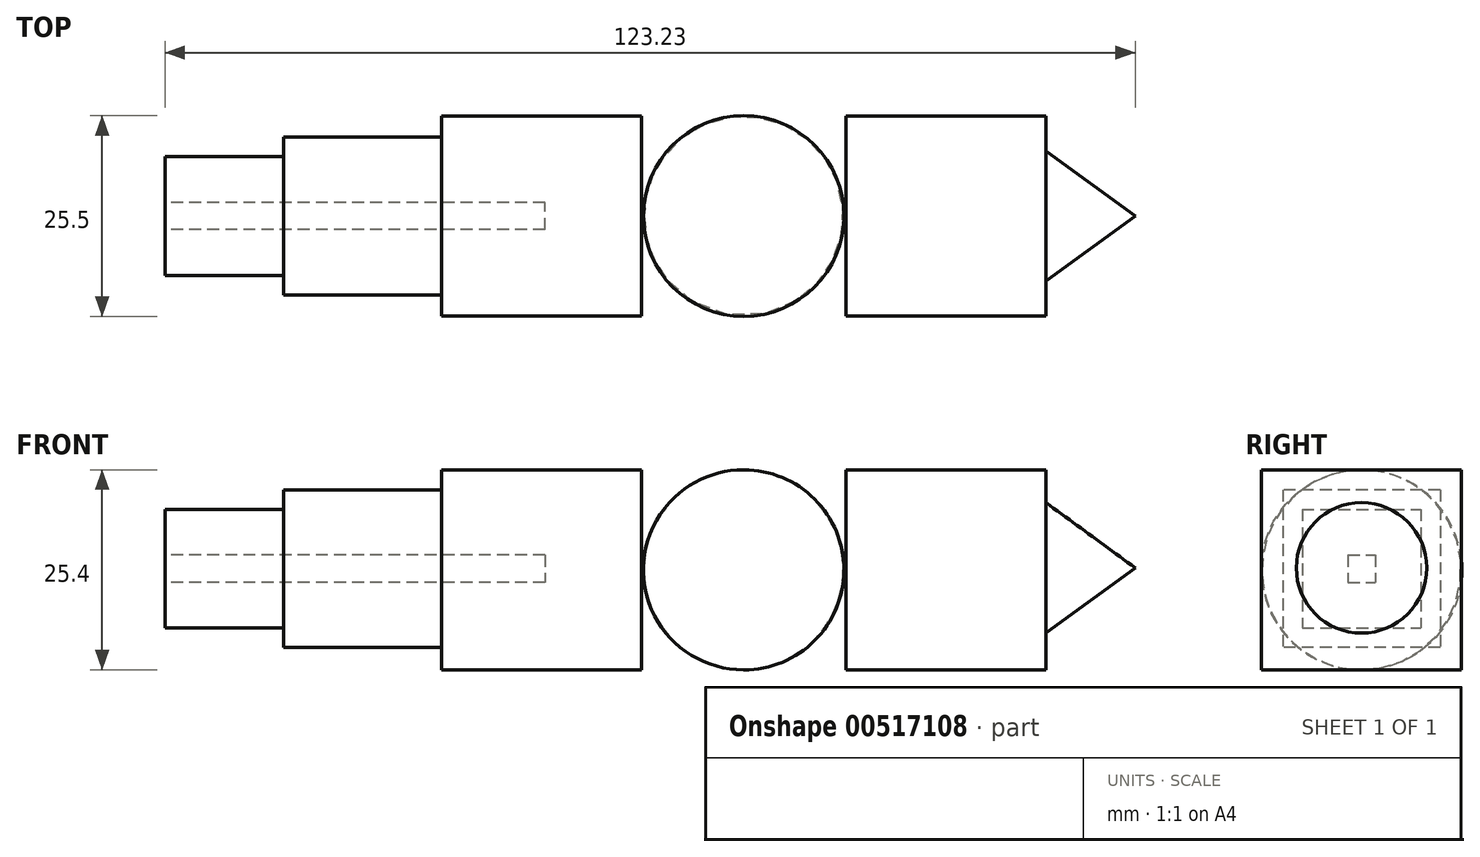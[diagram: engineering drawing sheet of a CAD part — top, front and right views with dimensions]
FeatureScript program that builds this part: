
annotation { "Feature Type Name" : "Feature", "Feature Type Description" : "" }
export const myFeature = defineFeature(function(context is Context, id is Id, definition is map)
    precondition{}
    {
        {
            var Q0;
            Q0=qCreatedBy(makeId("Front.planeOp"),FACE);
            var sketch = newSketch(context, id + "F0", { "sketchPlane" : qUnion([Q0])});
            skLineSegment(sketch, "E0.bottom", {"start": v(-38.4, 25.4) * mm, "end": v(-13, 25.4) * mm});
            skLineSegment(sketch, "E0.top", {"start": v(-38.4, 0) * mm, "end": v(-13, 0) * mm});
            skLineSegment(sketch, "E0.left", {"start": v(-38.4, 25.4) * mm, "end": v(-38.4, 0) * mm});
            skLineSegment(sketch, "E0.right", {"start": v(-13, 25.4) * mm, "end": v(-13, 0) * mm});
            skLineSegment(sketch, "E1", {"start": v(0, 25.4) * mm, "end": v(0, 0) * mm});
            skArc(sketch, "E2", {"start": v(0, 0) * mm, "mid": v(12.65, 12.7) * mm, "end": v(0, 25.4) * mm});
            skLineSegment(sketch, "E3.bottom", {"start": v(13, 25.4) * mm, "end": v(38.4, 25.4) * mm});
            skLineSegment(sketch, "E3.top", {"start": v(13, 0) * mm, "end": v(38.4, 0) * mm});
            skLineSegment(sketch, "E3.left", {"start": v(13, 25.4) * mm, "end": v(13, 0) * mm});
            skLineSegment(sketch, "E3.right", {"start": v(38.4, 25.4) * mm, "end": v(38.4, 0) * mm});
            skSolve(sketch);
        }
        {
            var Q0;
            Q0=makeQuery(id+"F0.imprint","IMPRINT",FACE,{"disambiguationData":[TD([[makeQuery(id+"F0.imprint","IMPRINT",EDGE,{"derivedFrom":sQuery(id+"F0.wireOp",EDGE,"E1")}),1.0]])]});
            var Q1;
            Q1=sQuery(id+"F0.wireOp",EDGE,"E1");
            revolve(context, id + "F1", {"entities" : qUnion([Q0]), "axis" : qUnion([Q1]), "revolveType" : RevolveType.FULL});
        }
        {
            var Q0;
            Q0=makeQuery(id+"F0.imprint","IMPRINT",FACE,{"disambiguationData":[TD([[makeQuery(id+"F0.imprint","IMPRINT",EDGE,{"derivedFrom":sQuery(id+"F0.wireOp",EDGE,"E0.bottom")}),-1.0]])]});
            extrude(context, id + "F2", {"entities" : qUnion([Q0]), "depth" : 12.7 * mm, "offsetDistance" : 25.4 * mm});
        }
        {
            var Q0;
            Q0=makeQuery(id+"F2.opExtrude","CAP_FACE",FACE,{"disambiguationData":[OSD([sQuery(id+"F0.wireOp",EDGE,"E0.bottom"),sQuery(id+"F0.wireOp",EDGE,"E0.top"),sQuery(id+"F0.wireOp",EDGE,"E0.left"),sQuery(id+"F0.wireOp",EDGE,"E0.right")])],"isStart":true});
            extrude(context, id + "F3", {"entities" : qUnion([Q0]), "operationType" : NewBodyOperationType.ADD, "depth" : 12.7 * mm, "offsetDistance" : 25.4 * mm});
        }
        {
            var Q0;
            Q0=makeQuery(id+"F0.imprint","IMPRINT",FACE,{"disambiguationData":[TD([[makeQuery(id+"F0.imprint","IMPRINT",EDGE,{"derivedFrom":sQuery(id+"F0.wireOp",EDGE,"E3.bottom")}),-1.0]])]});
            extrude(context, id + "F4", {"entities" : qUnion([Q0]), "depth" : 12.7 * mm, "offsetDistance" : 25.4 * mm});
        }
        {
            var Q0;
            Q0=makeQuery(id+"F4.opExtrude","CAP_FACE",FACE,{"disambiguationData":[OSD([sQuery(id+"F0.wireOp",EDGE,"E3.bottom"),sQuery(id+"F0.wireOp",EDGE,"E3.top"),sQuery(id+"F0.wireOp",EDGE,"E3.left"),sQuery(id+"F0.wireOp",EDGE,"E3.right")])],"isStart":true});
            extrude(context, id + "F5", {"entities" : qUnion([Q0]), "operationType" : NewBodyOperationType.ADD, "depth" : 12.7 * mm, "offsetDistance" : 25.4 * mm});
        }
        {
            var Q0;
            {var subQ0=sQuery(id+"F0.wireOp",EDGE,"E0.left");Q0=makeQuery(id+"F3.boolean.opBoolean","MERGE",FACE,{"derivedFrom":[makeQuery(id+"F2.opExtrude","SWEPT_FACE",FACE,{"disambiguationData":[OSD([subQ0])]}),makeQuery(id+"F3.opExtrude","SWEPT_FACE",FACE,{"disambiguationData":[OSD([subQ0])]})]});}
            var sketch = newSketch(context, id + "F6", { "sketchPlane" : qUnion([Q0])});
            skLineSegment(sketch, "E4.bottom", {"start": v(-10.01, 22.86) * mm, "end": v(10.01, 22.86) * mm});
            skLineSegment(sketch, "E4.top", {"start": v(-10.01, 2.84) * mm, "end": v(10.01, 2.84) * mm});
            skLineSegment(sketch, "E4.left", {"start": v(-10.01, 22.86) * mm, "end": v(-10.01, 2.84) * mm});
            skLineSegment(sketch, "E4.right", {"start": v(10.01, 22.86) * mm, "end": v(10.01, 2.84) * mm});
            skPoint(sketch, "E4.middle", {"position": v(0, 12.85) * mm});
            skSolve(sketch);
        }
        {
            var Q0;
            Q0=makeQuery(id+"F6.imprint","IMPRINT",FACE,{"disambiguationData":[TD([[makeQuery(id+"F6.imprint","IMPRINT",EDGE,{"derivedFrom":sQuery(id+"F6.wireOp",EDGE,"E4.bottom")}),-1.0]])]});
            extrude(context, id + "F7", {"entities" : qUnion([Q0]), "operationType" : NewBodyOperationType.ADD, "depth" : 20.02 * mm, "offsetDistance" : 25.4 * mm});
        }
        {
            var Q0;
            Q0=makeQuery(id+"F7.opExtrude","CAP_FACE",FACE,{"disambiguationData":[OSD([sQuery(id+"F6.wireOp",EDGE,"E4.bottom"),sQuery(id+"F6.wireOp",EDGE,"E4.top"),sQuery(id+"F6.wireOp",EDGE,"E4.left"),sQuery(id+"F6.wireOp",EDGE,"E4.right")])],"isStart":false});
            var sketch = newSketch(context, id + "F8", { "sketchPlane" : qUnion([Q0])});
            skLineSegment(sketch, "E5.bottom", {"start": v(7.54, 20.39) * mm, "end": v(-7.54, 20.39) * mm});
            skLineSegment(sketch, "E5.top", {"start": v(7.54, 5.32) * mm, "end": v(-7.54, 5.32) * mm});
            skLineSegment(sketch, "E5.left", {"start": v(7.54, 20.39) * mm, "end": v(7.54, 5.32) * mm});
            skLineSegment(sketch, "E5.right", {"start": v(-7.54, 20.39) * mm, "end": v(-7.54, 5.32) * mm});
            skPoint(sketch, "E5.middle", {"position": v(0, 12.85) * mm});
            skSolve(sketch);
        }
        {
            var Q0;
            Q0=makeQuery(id+"F8.imprint","IMPRINT",FACE,{"disambiguationData":[TD([[makeQuery(id+"F8.imprint","IMPRINT",EDGE,{"derivedFrom":sQuery(id+"F8.wireOp",EDGE,"E5.bottom")}),1.0]])]});
            extrude(context, id + "F9", {"entities" : qUnion([Q0]), "operationType" : NewBodyOperationType.ADD, "depth" : 15.07 * mm, "offsetDistance" : 25.4 * mm});
        }
        {
            var Q0;
            Q0=makeQuery(id+"F9.opExtrude","CAP_FACE",FACE,{"disambiguationData":[OSD([sQuery(id+"F8.wireOp",EDGE,"E5.bottom"),sQuery(id+"F8.wireOp",EDGE,"E5.top"),sQuery(id+"F8.wireOp",EDGE,"E5.left"),sQuery(id+"F8.wireOp",EDGE,"E5.right")])],"isStart":false});
            var sketch = newSketch(context, id + "F10", { "sketchPlane" : qUnion([Q0])});
            skLineSegment(sketch, "E6.bottom", {"start": v(1.73, 14.59) * mm, "end": v(-1.73, 14.59) * mm});
            skLineSegment(sketch, "E6.top", {"start": v(1.73, 11.12) * mm, "end": v(-1.73, 11.12) * mm});
            skLineSegment(sketch, "E6.left", {"start": v(1.73, 14.59) * mm, "end": v(1.73, 11.12) * mm});
            skLineSegment(sketch, "E6.right", {"start": v(-1.73, 14.59) * mm, "end": v(-1.73, 11.12) * mm});
            skPoint(sketch, "E6.middle", {"position": v(0, 12.85) * mm});
            skSolve(sketch);
        }
        {
            var Q0;
            Q0=makeQuery(id+"F10.imprint","IMPRINT",FACE,{"disambiguationData":[TD([[makeQuery(id+"F10.imprint","IMPRINT",EDGE,{"derivedFrom":sQuery(id+"F10.wireOp",EDGE,"E6.bottom")}),1.0]])]});
            extrude(context, id + "F11", {"entities" : qUnion([Q0]), "operationType" : NewBodyOperationType.REMOVE, "oppositeDirection" : true, "depth" : 48.26 * mm, "offsetDistance" : 25.4 * mm});
        }
        {
            var Q0;
            {var subQ0=sQuery(id+"F0.wireOp",EDGE,"E3.top");Q0=makeQuery(id+"F5.boolean.opBoolean","MERGE",FACE,{"derivedFrom":[makeQuery(id+"F4.opExtrude","SWEPT_FACE",FACE,{"disambiguationData":[OSD([subQ0])]}),makeQuery(id+"F5.opExtrude","SWEPT_FACE",FACE,{"disambiguationData":[OSD([subQ0])]})]});}
            var sketch = newSketch(context, id + "F12", { "sketchPlane" : qUnion([Q0])});
            skLineSegment(sketch, "E7", {"start": v(38.4, 0) * mm, "end": v(49.74, 0) * mm});
            skPoint(sketch, "E7.endSnap0", {"position": v(38.4, 0) * mm});
            skLineSegment(sketch, "E8", {"start": v(49.74, 0) * mm, "end": v(38.4, -8.29) * mm});
            skLineSegment(sketch, "E9", {"start": v(38.4, -8.29) * mm, "end": v(38.4, 0) * mm});
            skSolve(sketch);
        }
        {
            var Q0;
            Q0=makeQuery(id+"F12.imprint","IMPRINT",FACE,{"disambiguationData":[TD([[makeQuery(id+"F12.imprint","IMPRINT",EDGE,{"derivedFrom":sQuery(id+"F12.wireOp",EDGE,"E7")}),-1.0]])]});
            var Q1;
            Q1=sQuery(id+"F12.wireOp",EDGE,"E7");
            revolve(context, id + "F13", {"entities" : qUnion([Q0]), "axis" : qUnion([Q1]), "revolveType" : RevolveType.FULL});
        }
        {
            var Q0;
            Q0=makeQuery(id+"F13.opRevolve","SWEPT_BODY",BODY,{"disambiguationData":[OSD([sQuery(id+"F12.wireOp",EDGE,"E7"),sQuery(id+"F12.wireOp",EDGE,"E8"),sQuery(id+"F12.wireOp",EDGE,"E9")])]});
            transform(context, id + "F14", {"entities" : qUnion([Q0]), "transformType" : TransformType.TRANSLATION_3D, "dx" : 0 * mm, "dy" : 0 * mm, "dz" : 12.95 * mm, "makeCopy" : false});
        }
    });
